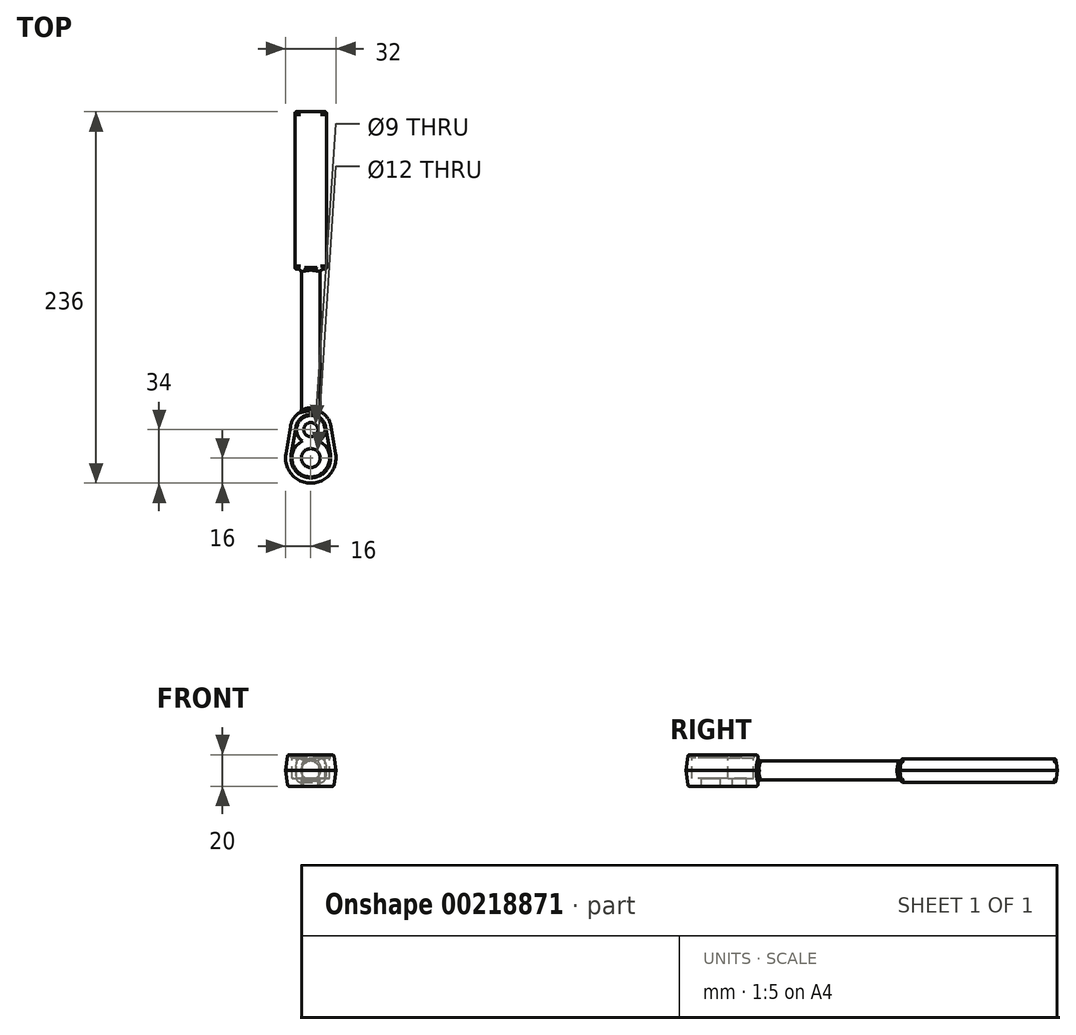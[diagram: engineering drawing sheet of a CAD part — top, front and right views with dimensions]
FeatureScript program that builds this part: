
annotation { "Feature Type Name" : "Feature", "Feature Type Description" : "" }
export const myFeature = defineFeature(function(context is Context, id is Id, definition is map)
    precondition{}
    {
        {
            var Q0;
            Q0=qCreatedBy(makeId("Top.planeOp"),FACE);
            var sketch = newSketch(context, id + "F0", { "sketchPlane" : qUnion([Q0])});
            skLineSegment(sketch, "E0", {"start": v(0, 0) * mm, "end": v(0, 220) * mm, "construction": true});
            skLineSegment(sketch, "E1", {"start": v(0, 220) * mm, "end": v(10, 220) * mm});
            skLineSegment(sketch, "E2", {"start": v(10, 220) * mm, "end": v(10, 120) * mm});
            skLineSegment(sketch, "E3", {"start": v(10, 120) * mm, "end": v(0, 120) * mm});
            skLineSegment(sketch, "E4.MirrorCS", {"start": v(-10, 120) * mm, "end": v(0, 120) * mm});
            skLineSegment(sketch, "E5.MirrorCS", {"start": v(0, 220) * mm, "end": v(-10, 220) * mm});
            skLineSegment(sketch, "E6.MirrorCS", {"start": v(-10, 220) * mm, "end": v(-10, 120) * mm});
            skSolve(sketch);
        }
        {
            var Q0;
            Q0=makeQuery(id+"F0.imprint","IMPRINT",FACE,{"disambiguationData":[TD([[makeQuery(id+"F0.imprint","IMPRINT",EDGE,{"derivedFrom":sQuery(id+"F0.wireOp",EDGE,"E1")}),-1.0]])]});
            extrude(context, id + "F1", {"entities" : qUnion([Q0]), "endBound" : BoundingType.SYMMETRIC, "depth" : 15 * mm, "hasDraft" : true, "draftAngle" : 8 * degree, "draftPullDirection" : true});
        }
        {
            var Q0;
            Q0=qCreatedBy(makeId("Front.planeOp"),FACE);
            var sketch = newSketch(context, id + "F2", { "sketchPlane" : qUnion([Q0])});
            skCircle(sketch, "E7", {"center": v(0, 0) * mm, "radius": 6 * mm});
            skSolve(sketch);
        }
        {
            var Q0;
            Q0 = qSketchRegion(id + "F2", true);
            extrude(context, id + "F3", {"entities" : qUnion([Q0]), "operationType" : NewBodyOperationType.ADD, "endBound" : BoundingType.UP_TO_NEXT, "oppositeDirection" : true, "depth" : 25 * mm});
        }
        {
            var Q0;
            Q0=qCreatedBy(makeId("Top.planeOp"),FACE);
            var sketch = newSketch(context, id + "F4", { "sketchPlane" : qUnion([Q0])});
            skLineSegment(sketch, "E8", {"start": v(0, 0) * mm, "end": v(0, 18) * mm, "construction": true});
            skLineSegment(sketch, "E9", {"start": v(-15.78, 2.67) * mm, "end": v(-12.82, 20.17) * mm});
            skArc(sketch, "E10", {"start": v(12.82, 20.17) * mm, "mid": v(0, 31) * mm, "end": v(-12.82, 20.17) * mm});
            skLineSegment(sketch, "E11", {"start": v(12.82, 20.17) * mm, "end": v(15.78, 2.67) * mm});
            skArc(sketch, "E12", {"start": v(-15.78, 2.67) * mm, "mid": v(0, -16) * mm, "end": v(15.78, 2.67) * mm});
            skSolve(sketch);
        }
        {
            var Q0;
            Q0=makeQuery(id+"F4.imprint","IMPRINT",FACE,{"disambiguationData":[TD([[makeQuery(id+"F4.imprint","IMPRINT",EDGE,{"derivedFrom":sQuery(id+"F4.wireOp",EDGE,"E9")}),-1.0]])]});
            extrude(context, id + "F5", {"entities" : qUnion([Q0]), "operationType" : NewBodyOperationType.ADD, "endBound" : BoundingType.SYMMETRIC, "depth" : 20 * mm, "hasDraft" : true, "draftAngle" : 8 * degree, "draftPullDirection" : true});
        }
        {
            var Q0;
            Q0=makeQuery(id+"F5.opExtrude","CAP_FACE",FACE,{"disambiguationData":[OSD([sQuery(id+"F4.wireOp",EDGE,"E9"),sQuery(id+"F4.wireOp",EDGE,"E10"),sQuery(id+"F4.wireOp",EDGE,"E11"),sQuery(id+"F4.wireOp",EDGE,"E12")])],"isStart":false});
            var sketch = newSketch(context, id + "F6", { "sketchPlane" : qUnion([Q0])});
            skArc(sketch, "E13.0", {"start": v(9.46, 19.6) * mm, "mid": v(0, 27.6) * mm, "end": v(-9.46, 19.6) * mm});
            skLineSegment(sketch, "E13.1", {"start": v(9.46, 19.6) * mm, "end": v(12.42, 2.1) * mm});
            skArc(sketch, "E13.2", {"start": v(-12.42, 2.1) * mm, "mid": v(0, -12.6) * mm, "end": v(12.42, 2.1) * mm});
            skLineSegment(sketch, "E13.3", {"start": v(-12.42, 2.1) * mm, "end": v(-9.46, 19.6) * mm});
            skSolve(sketch);
        }
        {
            var Q0;
            Q0=makeQuery(id+"F6.imprint","IMPRINT",FACE,{"disambiguationData":[TD([[makeQuery(id+"F6.imprint","IMPRINT",EDGE,{"derivedFrom":sQuery(id+"F6.wireOp",EDGE,"E13.0")}),1.0]])]});
            extrude(context, id + "F7", {"entities" : qUnion([Q0]), "operationType" : NewBodyOperationType.REMOVE, "oppositeDirection" : true, "depth" : 2 * mm});
        }
        {
            var Q0;
            Q0=makeQuery(id+"F5.opExtrude","CAP_FACE",FACE,{"disambiguationData":[OSD([sQuery(id+"F4.wireOp",EDGE,"E9"),sQuery(id+"F4.wireOp",EDGE,"E10"),sQuery(id+"F4.wireOp",EDGE,"E11"),sQuery(id+"F4.wireOp",EDGE,"E12")])],"isStart":true});
            cPlane(context, id + "F8", {"entities" : qUnion([Q0]), "cplaneType" : CPlaneType.OFFSET, "offset" : 5 * mm, "oppositeDirection" : true, "width" : 150 * mm, "height" : 150 * mm});
        }
        {
            var Q0;
            Q0=makeQuery(id+"F7.boolean.opBoolean","COPY",FACE,{"derivedFrom":makeQuery(id+"F7.opExtrude","CAP_FACE",FACE,{"disambiguationData":[OSD([sQuery(id+"F6.wireOp",EDGE,"E13.0"),sQuery(id+"F6.wireOp",EDGE,"E13.1"),sQuery(id+"F6.wireOp",EDGE,"E13.2"),sQuery(id+"F6.wireOp",EDGE,"E13.3")])],"isStart":false})});
            var sketch = newSketch(context, id + "F9", { "sketchPlane" : qUnion([Q0])});
            skPoint(sketch, "E14", {"position": v(0, 18) * mm});
            skPoint(sketch, "E15", {"position": v(0, 0) * mm});
            skArc(sketch, "E16", {"start": v(5.33, 10.75) * mm, "mid": v(0, 27) * mm, "end": v(-5.33, 10.75) * mm});
            skArc(sketch, "E17", {"start": v(-5.33, 10.75) * mm, "mid": v(0, -12) * mm, "end": v(5.33, 10.75) * mm});
            skSolve(sketch);
        }
        {
            var Q0;
            Q0=makeQuery(id+"F9.imprint","IMPRINT",FACE,{"disambiguationData":[TD([[makeQuery(id+"F9.imprint","IMPRINT",EDGE,{"derivedFrom":sQuery(id+"F9.wireOp",EDGE,"E16")}),1.0]])]});
            var Q1;
            Q1=qCreatedBy(id+"F8.planeOp",FACE);
            extrude(context, id + "F10", {"entities" : qUnion([Q0]), "operationType" : NewBodyOperationType.REMOVE, "endBound" : BoundingType.UP_TO_SURFACE, "oppositeDirection" : true, "endBoundEntityFace" : qUnion([Q1]), "depth" : 25 * mm});
        }
        {
            var Q0;
            Q0=makeQuery(id+"F10.boolean.opBoolean","COPY",FACE,{"derivedFrom":makeQuery(id+"F10.opExtrude","CAP_FACE",FACE,{"disambiguationData":[OSD([sQuery(id+"F9.wireOp",EDGE,"E16"),sQuery(id+"F9.wireOp",EDGE,"E17")])],"isStart":false})});
            var sketch = newSketch(context, id + "F11", { "sketchPlane" : qUnion([Q0])});
            skPoint(sketch, "E18", {"position": v(0, 18) * mm});
            skPoint(sketch, "E19", {"position": v(0, 0) * mm});
            skSolve(sketch);
        }
        {
            var Q0;
            Q0=sQuery(id+"F11.wireOp",VERTEX,"E18");
            var Q1;
            Q1=makeQuery(id+"F1.split0.splitOp","SPLIT",BODY,{"derivedFrom":makeQuery(id+"F1.opExtrude","SWEPT_BODY",BODY,{"disambiguationData":[OSD([sQuery(id+"F0.wireOp",EDGE,"E1"),sQuery(id+"F0.wireOp",EDGE,"E2"),sQuery(id+"F0.wireOp",EDGE,"E3"),sQuery(id+"F0.wireOp",EDGE,"E4.MirrorCS"),sQuery(id+"F0.wireOp",EDGE,"E5.MirrorCS"),sQuery(id+"F0.wireOp",EDGE,"E6.MirrorCS")])]})});
            hole(context, id + "F12", {"style" : HoleStyle.SIMPLE, "endStyle" : HoleEndStyle.THROUGH, "holeDiameter" : 9 * mm, "locations" : qUnion([Q0]), "scope" : qUnion([Q1]), "isTappedThrough" : true});
        }
        {
            var Q0;
            Q0=sQuery(id+"F11.wireOp",VERTEX,"E19");
            var Q1;
            Q1=makeQuery(id+"F1.split0.splitOp","SPLIT",BODY,{"derivedFrom":makeQuery(id+"F1.opExtrude","SWEPT_BODY",BODY,{"disambiguationData":[OSD([sQuery(id+"F0.wireOp",EDGE,"E1"),sQuery(id+"F0.wireOp",EDGE,"E2"),sQuery(id+"F0.wireOp",EDGE,"E3"),sQuery(id+"F0.wireOp",EDGE,"E4.MirrorCS"),sQuery(id+"F0.wireOp",EDGE,"E5.MirrorCS"),sQuery(id+"F0.wireOp",EDGE,"E6.MirrorCS")])]})});
            hole(context, id + "F13", {"style" : HoleStyle.SIMPLE, "endStyle" : HoleEndStyle.THROUGH, "holeDiameter" : 12 * mm, "locations" : qUnion([Q0]), "scope" : qUnion([Q1]), "isTappedThrough" : true});
        }
        {
            var Q0;
            Q0=makeQuery(id+"F1.opExtrude","CAP_EDGE",EDGE,{"disambiguationData":[OSD([sQuery(id+"F0.wireOp",EDGE,"E6.MirrorCS")])],"isStart":false});
            var Q1;
            Q1=makeQuery(id+"F1.opExtrude","CAP_EDGE",EDGE,{"disambiguationData":[OSD([sQuery(id+"F0.wireOp",EDGE,"E6.MirrorCS")])],"isStart":true});
            var Q2;
            Q2=makeQuery(id+"F1.opExtrude","CAP_EDGE",EDGE,{"disambiguationData":[OSD([sQuery(id+"F0.wireOp",EDGE,"E2")])],"isStart":true});
            var Q3;
            Q3=makeQuery(id+"F1.opExtrude","CAP_EDGE",EDGE,{"disambiguationData":[OSD([sQuery(id+"F0.wireOp",EDGE,"E2")])],"isStart":false});
            fillet(context, id + "F14", {"entities" : qUnion([Q0, Q1, Q2, Q3]), "radius" : 3 * mm, "tangentPropagation" : true, "allowEdgeOverflow" : false});
        }
        {
            var Q0;
            Q0=makeQuery(id+"F1.split0.splitOp","SPLIT",EDGE,{"derivedFrom":makeQuery(id+"F1.opExtrude","SWEPT_EDGE",EDGE,{"disambiguationData":[OSD([sQuery(id+"F0.wireOp",EDGE,"E4.MirrorCS"),sQuery(id+"F0.wireOp",EDGE,"E6.MirrorCS")])]}),"isFromBackBody":true});
            var Q1;
            Q1=makeQuery(id+"F1.split0.splitOp","SPLIT",EDGE,{"derivedFrom":makeQuery(id+"F1.opExtrude","SWEPT_EDGE",EDGE,{"disambiguationData":[OSD([sQuery(id+"F0.wireOp",EDGE,"E4.MirrorCS"),sQuery(id+"F0.wireOp",EDGE,"E6.MirrorCS")])]})});
            var Q2;
            Q2=makeQuery(id+"F1.split0.splitOp","SPLIT",EDGE,{"derivedFrom":makeQuery(id+"F1.opExtrude","SWEPT_EDGE",EDGE,{"disambiguationData":[OSD([sQuery(id+"F0.wireOp",EDGE,"E5.MirrorCS"),sQuery(id+"F0.wireOp",EDGE,"E6.MirrorCS")])]})});
            var Q3;
            Q3=makeQuery(id+"F1.split0.splitOp","SPLIT",EDGE,{"derivedFrom":makeQuery(id+"F1.opExtrude","SWEPT_EDGE",EDGE,{"disambiguationData":[OSD([sQuery(id+"F0.wireOp",EDGE,"E5.MirrorCS"),sQuery(id+"F0.wireOp",EDGE,"E6.MirrorCS")])]}),"isFromBackBody":true});
            var Q4;
            Q4=makeQuery(id+"F5.opExtrude","CAP_EDGE",EDGE,{"disambiguationData":[OSD([sQuery(id+"F4.wireOp",EDGE,"E9")])],"isStart":false});
            var Q5;
            Q5=makeQuery(id+"F5.opExtrude","CAP_EDGE",EDGE,{"disambiguationData":[OSD([sQuery(id+"F4.wireOp",EDGE,"E9")])],"isStart":true});
            fillet(context, id + "F15", {"entities" : qUnion([Q0, Q1, Q2, Q3, Q4, Q5]), "radius" : 1 * mm, "tangentPropagation" : true, "allowEdgeOverflow" : false});
        }
        {
            var Q0;
            Q0=makeQuery(id+"F3.opExtrude","SWEPT_FACE",FACE,{"disambiguationData":[OSD([sQuery(id+"F2.wireOp",EDGE,"E7")])]});
            fillet(context, id + "F16", {"entities" : qUnion([Q0]), "radius" : 2 * mm, "tangentPropagation" : true, "allowEdgeOverflow" : false});
        }
    });
